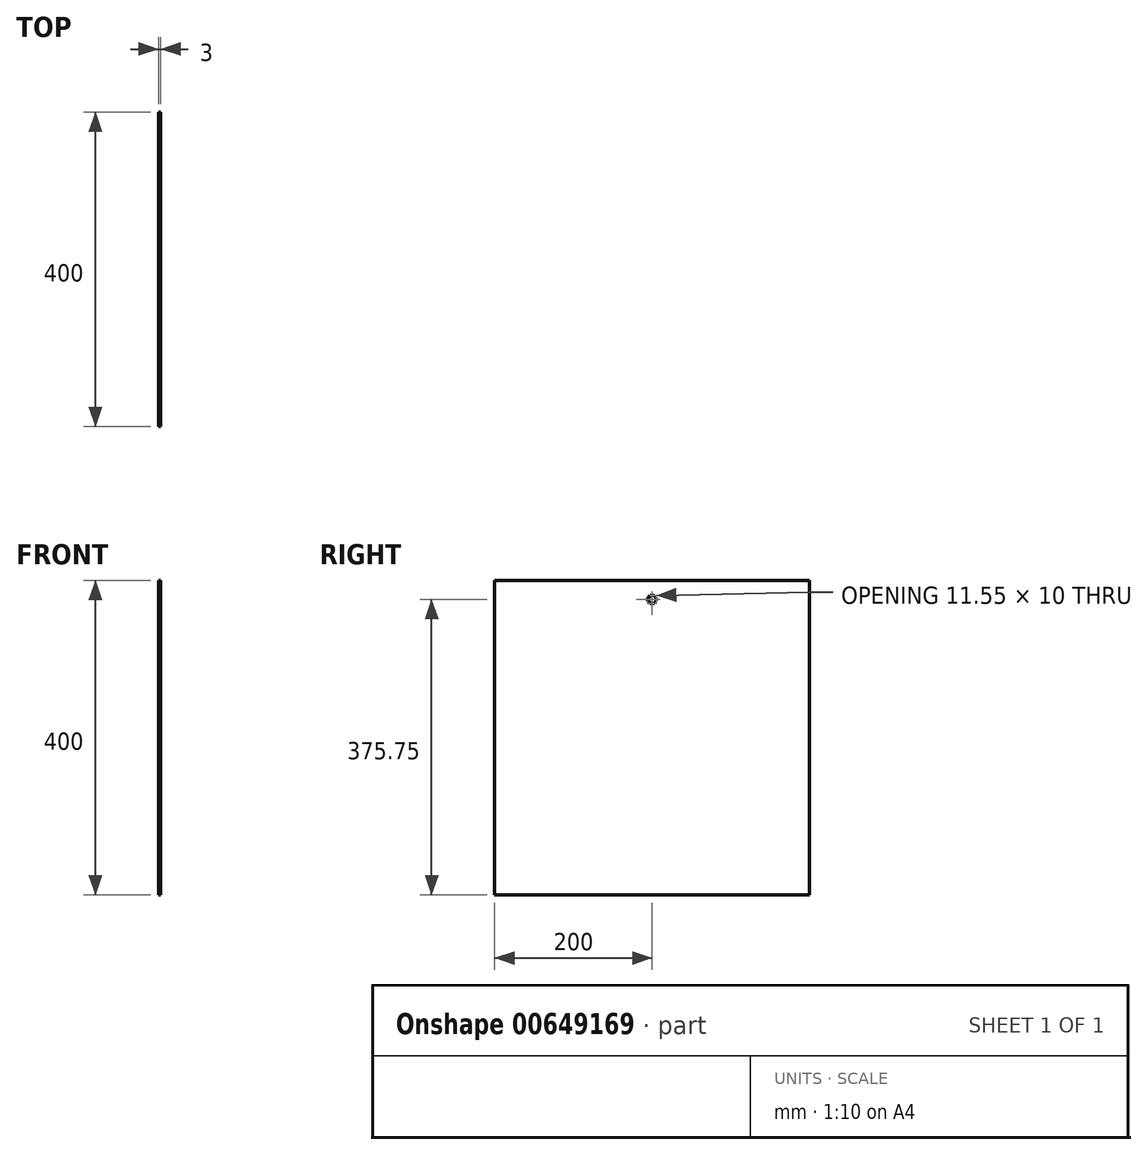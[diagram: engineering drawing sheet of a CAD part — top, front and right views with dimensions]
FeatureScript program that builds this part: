
annotation { "Feature Type Name" : "Feature", "Feature Type Description" : "" }
export const myFeature = defineFeature(function(context is Context, id is Id, definition is map)
    precondition{}
    {
        {
            var Q0;
            Q0=qCreatedBy(makeId("Right.planeOp"),FACE);
            var sketch = newSketch(context, id + "F0", { "sketchPlane" : qUnion([Q0])});
            skLineSegment(sketch, "E0.bottom", {"start": v(200, 200) * mm, "end": v(-200, 200) * mm});
            skLineSegment(sketch, "E0.top", {"start": v(200, -200) * mm, "end": v(-200, -200) * mm});
            skLineSegment(sketch, "E0.left", {"start": v(200, 200) * mm, "end": v(200, -200) * mm});
            skLineSegment(sketch, "E0.right", {"start": v(-200, 200) * mm, "end": v(-200, -200) * mm});
            skPoint(sketch, "E0.middle", {"position": v(0, 0) * mm});
            skSolve(sketch);
        }
        {
            var Q0;
            Q0 = qSketchRegion(id + "F0", true);
            extrude(context, id + "F1", {"entities" : qUnion([Q0]), "depth" : 3 * mm, "offsetDistance" : 25 * mm});
        }
        {
            var Q0;
            Q0=makeQuery(id+"F1.opExtrude","CAP_FACE",FACE,{"disambiguationData":[OSD([sQuery(id+"F0.wireOp",EDGE,"E0.bottom"),sQuery(id+"F0.wireOp",EDGE,"E0.top"),sQuery(id+"F0.wireOp",EDGE,"E0.left"),sQuery(id+"F0.wireOp",EDGE,"E0.right")])],"isStart":false});
            var sketch = newSketch(context, id + "F2", { "sketchPlane" : qUnion([Q0])});
            skLineSegment(sketch, "E1", {"start": v(0, 200) * mm, "end": v(0, 175.75) * mm, "construction": true});
            skCircle(sketch, "E2.cCircle", {"center": v(0, 175.75) * mm, "radius": 5 * mm, "construction": true});
            skLineSegment(sketch, "E2.0", {"start": v(-2.89, 180.75) * mm, "end": v(2.89, 180.75) * mm});
            skLineSegment(sketch, "E2.1", {"start": v(2.89, 180.75) * mm, "end": v(5.77, 175.75) * mm});
            skLineSegment(sketch, "E2.2", {"start": v(5.77, 175.75) * mm, "end": v(2.89, 170.75) * mm});
            skLineSegment(sketch, "E2.3", {"start": v(2.89, 170.75) * mm, "end": v(-2.89, 170.75) * mm});
            skLineSegment(sketch, "E2.4", {"start": v(-2.89, 170.75) * mm, "end": v(-5.77, 175.75) * mm});
            skLineSegment(sketch, "E2.5", {"start": v(-5.77, 175.75) * mm, "end": v(-2.89, 180.75) * mm});
            skPoint(sketch, "E2.0.midPoint", {"position": v(0, 180.75) * mm});
            skSolve(sketch);
        }
        {
            var Q0;
            Q0 = qSketchRegion(id + "F2", true);
            extrude(context, id + "F3", {"entities" : qUnion([Q0]), "operationType" : NewBodyOperationType.REMOVE, "oppositeDirection" : true, "depth" : 25 * mm, "offsetDistance" : 25 * mm});
        }
    });
